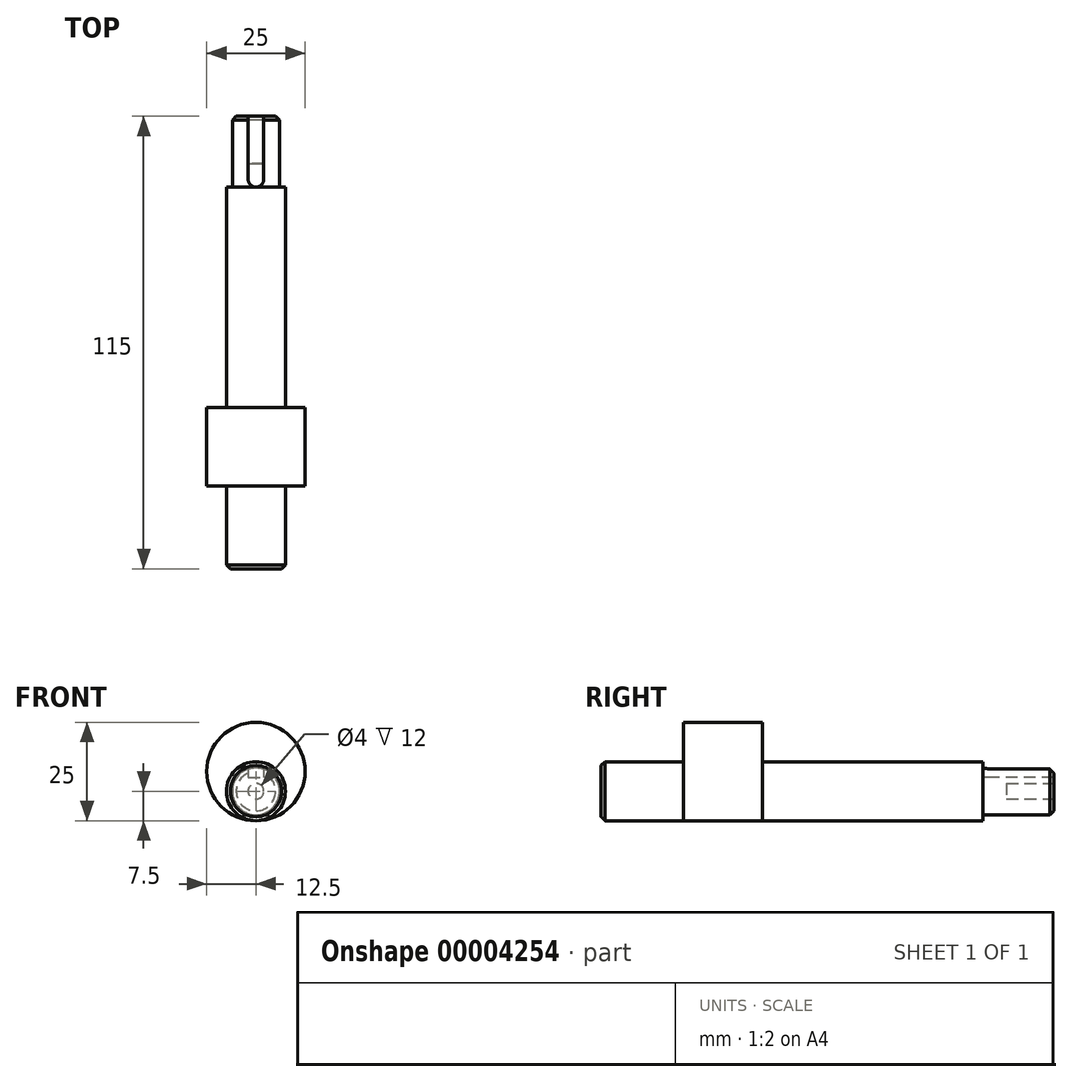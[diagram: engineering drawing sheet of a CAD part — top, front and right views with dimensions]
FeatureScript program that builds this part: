
annotation { "Feature Type Name" : "Feature", "Feature Type Description" : "" }
export const myFeature = defineFeature(function(context is Context, id is Id, definition is map)
    precondition{}
    {
        {
            var Q0;
            Q0=qCreatedBy(makeId("Front.planeOp"),FACE);
            var sketch = newSketch(context, id + "F0", { "sketchPlane" : qUnion([Q0])});
            skCircle(sketch, "E0", {"center": v(0, 0) * mm, "radius": 7.5 * mm});
            skSolve(sketch);
        }
        {
            var Q0;
            Q0 = qSketchRegion(id + "F0", true);
            extrude(context, id + "F1", {"entities" : qUnion([Q0]), "oppositeDirection" : true, "depth" : (21 + 20 + 74 - 18) * mm});
        }
        {
            var Q0;
            Q0=makeQuery(id+"F1.opExtrude","CAP_FACE",FACE,{"disambiguationData":[OSD([sQuery(id+"F0.wireOp",EDGE,"E0")])],"isStart":false});
            var sketch = newSketch(context, id + "F2", { "sketchPlane" : qUnion([Q0])});
            skCircle(sketch, "E1", {"center": v(0, 0) * mm, "radius": 6 * mm});
            skSolve(sketch);
        }
        {
            var Q0;
            Q0 = qSketchRegion(id + "F2", true);
            extrude(context, id + "F3", {"entities" : qUnion([Q0]), "operationType" : NewBodyOperationType.ADD, "depth" : 18 * mm});
        }
        {
            var Q0;
            Q0=qCreatedBy(makeId("Front.planeOp"),FACE);
            cPlane(context, id + "F4", {"entities" : qUnion([Q0]), "cplaneType" : CPlaneType.OFFSET, "offset" : 21 * mm, "oppositeDirection" : true, "width" : 150 * mm, "height" : 150 * mm});
        }
        {
            var Q0;
            Q0=qCreatedBy(id+"F4.planeOp",FACE);
            var sketch = newSketch(context, id + "F5", { "sketchPlane" : qUnion([Q0])});
            skCircle(sketch, "E2", {"center": v(0, 5) * mm, "radius": 12.5 * mm});
            skSolve(sketch);
        }
        {
            var Q0;
            Q0 = qSketchRegion(id + "F5", true);
            extrude(context, id + "F6", {"entities" : qUnion([Q0]), "operationType" : NewBodyOperationType.ADD, "oppositeDirection" : true, "depth" : 20 * mm});
        }
        {
            var Q0;
            Q0=makeQuery(id+"F1.opExtrude","CAP_EDGE",EDGE,{"disambiguationData":[OSD([sQuery(id+"F0.wireOp",EDGE,"E0")])],"isStart":true});
            var Q1;
            Q1=makeQuery(id+"F3.opExtrude","CAP_EDGE",EDGE,{"disambiguationData":[OSD([sQuery(id+"F2.wireOp",EDGE,"E1")])],"isStart":false});
            chamfer(context, id + "F7", {"entities" : qUnion([Q0, Q1]), "width" : 1 * mm, "tangentPropagation" : true});
        }
        {
            var Q0;
            Q0=makeQuery(id+"F3.opExtrude","CAP_FACE",FACE,{"disambiguationData":[OSD([sQuery(id+"F2.wireOp",EDGE,"E1")])],"isStart":false});
            var sketch = newSketch(context, id + "F8", { "sketchPlane" : qUnion([Q0])});
            skCircle(sketch, "E3", {"center": v(0, 0) * mm, "radius": 2 * mm});
            skSolve(sketch);
        }
        {
            var Q0;
            Q0 = qSketchRegion(id + "F8", true);
            extrude(context, id + "F9", {"entities" : qUnion([Q0]), "operationType" : NewBodyOperationType.REMOVE, "oppositeDirection" : true, "depth" : 12 * mm});
        }
        {
            var Q0;
            Q0=qCreatedBy(makeId("Top.planeOp"),FACE);
            cPlane(context, id + "F10", {"entities" : qUnion([Q0]), "cplaneType" : CPlaneType.OFFSET, "offset" : 3.5 * mm, "width" : 150 * mm, "height" : 150 * mm});
        }
        {
            var Q0;
            Q0=qCreatedBy(id+"F10.planeOp",FACE);
            var sketch = newSketch(context, id + "F11", { "sketchPlane" : qUnion([Q0])});
            skLineSegment(sketch, "E4", {"start": v(-2, 115) * mm, "end": v(-2, 99) * mm});
            skLineSegment(sketch, "E5", {"start": v(-2, 115) * mm, "end": v(2, 115) * mm});
            skLineSegment(sketch, "E6", {"start": v(2, 115) * mm, "end": v(2, 99) * mm});
            skArc(sketch, "E7", {"start": v(-2, 99) * mm, "mid": v(0, 97) * mm, "end": v(2, 99) * mm});
            skSolve(sketch);
        }
        {
            var Q0;
            Q0 = qSketchRegion(id + "F11", true);
            extrude(context, id + "F12", {"entities" : qUnion([Q0]), "operationType" : NewBodyOperationType.REMOVE, "endBound" : BoundingType.THROUGH_ALL, "depth" : 25 * mm});
        }
    });
